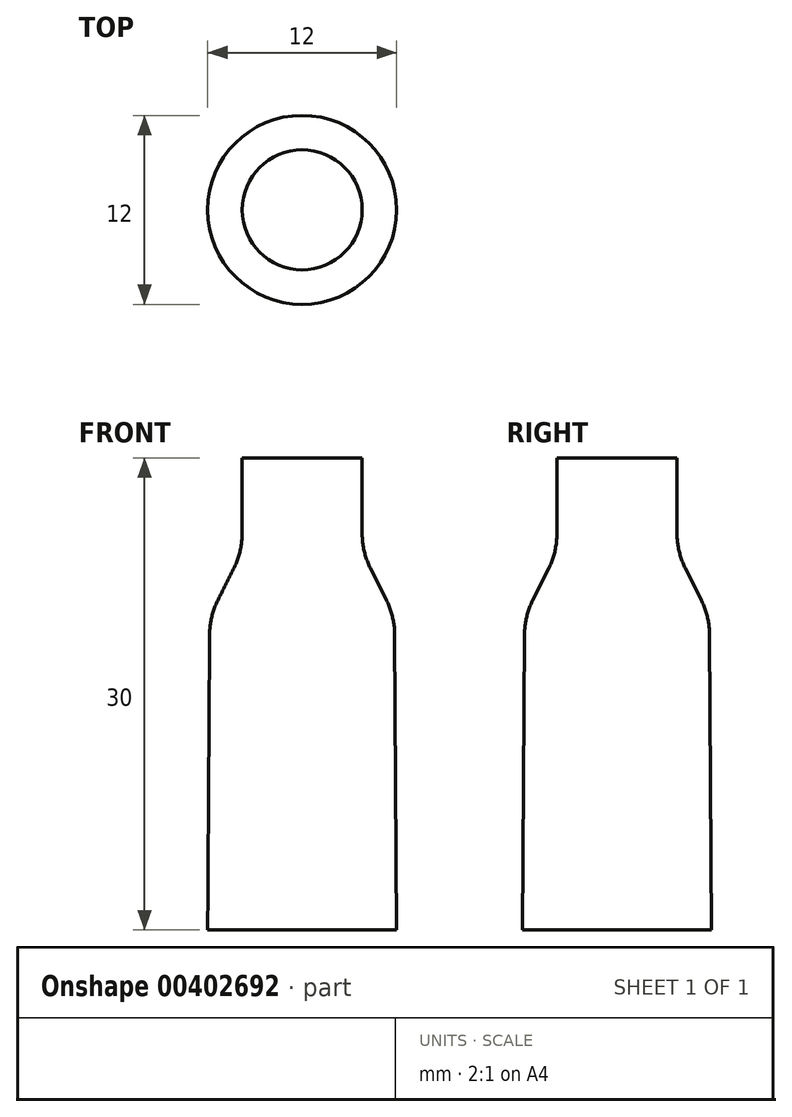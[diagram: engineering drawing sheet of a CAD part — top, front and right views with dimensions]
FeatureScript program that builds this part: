
annotation { "Feature Type Name" : "Feature", "Feature Type Description" : "" }
export const myFeature = defineFeature(function(context is Context, id is Id, definition is map)
    precondition{}
    {
        {
            var Q0;
            Q0=qCreatedBy(makeId("Front.planeOp"),FACE);
            var sketch = newSketch(context, id + "F0", { "sketchPlane" : qUnion([Q0])});
            skLineSegment(sketch, "E0", {"start": v(0, 0) * mm, "end": v(0, -30) * mm});
            skLineSegment(sketch, "E1", {"start": v(0, 0) * mm, "end": v(3.81, 0) * mm});
            skLineSegment(sketch, "E2", {"start": v(0, -30) * mm, "end": v(6, -30) * mm});
            skLineSegment(sketch, "E3", {"start": v(3.81, 0) * mm, "end": v(3.81, -4.78) * mm});
            skLineSegment(sketch, "E4", {"start": v(4.34, -7) * mm, "end": v(5.36, -9.05) * mm});
            skLineSegment(sketch, "E5", {"start": v(6, -30) * mm, "end": v(5.88, -11.25) * mm});
            skPoint(sketch, "E6.visualSharp", {"position": v(3.81, -5.96) * mm});
            skArc(sketch, "E6.filletArc", {"start": v(3.81, -4.78) * mm, "mid": v(3.95, -5.92) * mm, "end": v(4.34, -7) * mm});
            skPoint(sketch, "E7.visualSharp", {"position": v(5.87, -10.09) * mm});
            skArc(sketch, "E7.filletArc", {"start": v(5.88, -11.25) * mm, "mid": v(5.74, -10.12) * mm, "end": v(5.36, -9.05) * mm});
            skSolve(sketch);
        }
        {
            var Q0;
            Q0=makeQuery(id+"F0.imprint","IMPRINT",FACE,{"disambiguationData":[TD([[makeQuery(id+"F0.imprint","IMPRINT",EDGE,{"derivedFrom":sQuery(id+"F0.wireOp",EDGE,"E0")}),1.0]])]});
            var Q1;
            Q1=sQuery(id+"F0.wireOp",EDGE,"E3");
            var Q2;
            Q2=sQuery(id+"F0.wireOp",EDGE,"E6.filletArc");
            var Q3;
            Q3=sQuery(id+"F0.wireOp",EDGE,"E4");
            var Q4;
            Q4=sQuery(id+"F0.wireOp",EDGE,"E5");
            var Q5;
            Q5=sQuery(id+"F0.wireOp",EDGE,"E7.filletArc");
            var Q6;
            Q6=sQuery(id+"F0.wireOp",EDGE,"E0");
            revolve(context, id + "F1", {"bodyType" : ToolBodyType.SURFACE, "entities" : qUnion([Q0]), "surfaceEntities" : qUnion([Q1, Q2, Q3, Q4, Q5]), "axis" : qUnion([Q6]), "revolveType" : RevolveType.FULL});
        }
    });
